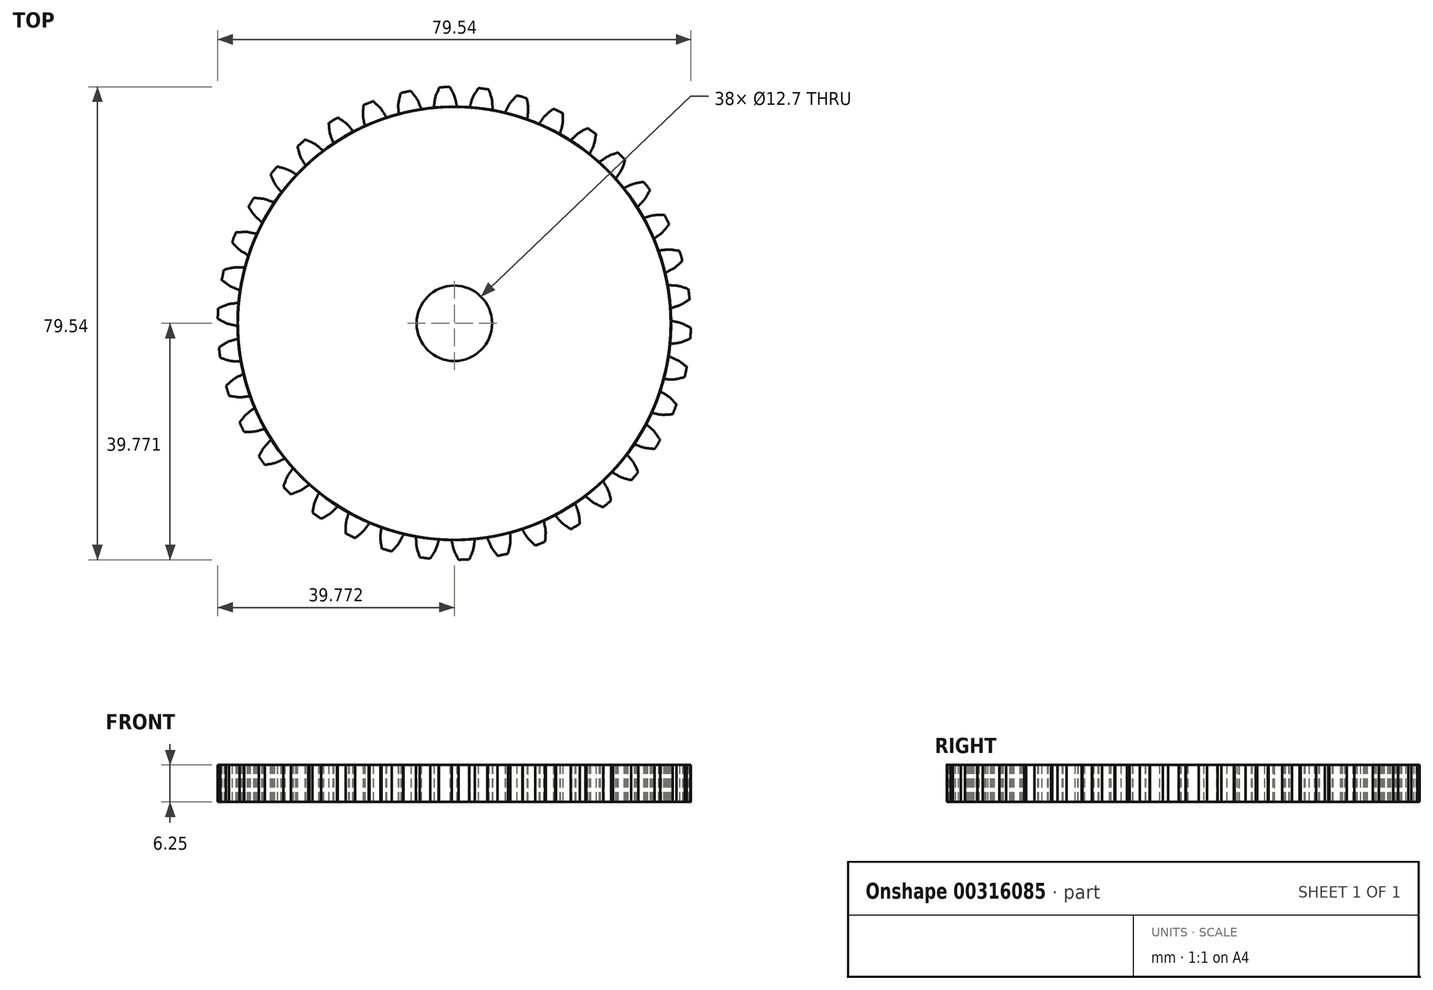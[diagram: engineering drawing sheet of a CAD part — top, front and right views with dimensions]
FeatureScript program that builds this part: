
annotation { "Feature Type Name" : "Feature", "Feature Type Description" : "" }
export const myFeature = defineFeature(function(context is Context, id is Id, definition is map)
    precondition{}
    {
        {
            var Q0;
            Q0=qCreatedBy(makeId("Top.planeOp"),FACE);
            var sketch = newSketch(context, id + "F0", { "sketchPlane" : qUnion([Q0])});
            skCircle(sketch, "E0", {"center": v(0, 0) * mm, "radius": 38.1 * mm, "construction": true});
            skLineSegment(sketch, "E1", {"start": v(0, 0) * mm, "end": v(0, 54.47) * mm, "construction": true});
            skLineSegment(sketch, "E2", {"start": v(-40.8, 38.1) * mm, "end": v(45.04, 38.1) * mm, "construction": true});
            skLineSegment(sketch, "E3", {"start": v(-12.24, 33.64) * mm, "end": v(18.8, 44.94) * mm, "construction": true});
            skLineSegment(sketch, "E4", {"start": v(0, 0) * mm, "end": v(-12.24, 33.64) * mm, "construction": true});
            skCircle(sketch, "E5", {"center": v(0, 0) * mm, "radius": 35.8 * mm, "construction": true});
            skPoint(sketch, "E6", {"position": v(-12.24, 33.64) * mm});
            skPoint(sketch, "E7", {"position": v(0, 38.1) * mm});
            skPoint(sketch, "E8", {"position": v(-16.8, 31.61) * mm});
            skLineSegment(sketch, "E9", {"start": v(-16.8, 31.61) * mm, "end": v(-0.9, 40.1) * mm, "construction": true});
            skArc(sketch, "E10", {"start": v(-7.44, 35.02) * mm, "mid": v(-9.87, 34.42) * mm, "end": v(-12.24, 33.64) * mm});
            skArc(sketch, "E11", {"start": v(-12.24, 33.64) * mm, "mid": v(-14.56, 32.7) * mm, "end": v(-16.8, 31.61) * mm});
            skLineSegment(sketch, "E12", {"start": v(-7.44, 35.02) * mm, "end": v(0.41, 36.69) * mm, "construction": true});
            skLineSegment(sketch, "E13", {"start": v(0, 38.1) * mm, "end": v(0, 0) * mm, "construction": true});
            skLineSegment(sketch, "E14", {"start": v(0.41, 36.69) * mm, "end": v(0.43, 36.44) * mm});
            skLineSegment(sketch, "E15.trimOffspring", {"start": v(0, 36.44) * mm, "end": v(0, 36.44) * mm});
            skLineSegment(sketch, "E16", {"start": v(0, 0) * mm, "end": v(-1.9, 46.38) * mm, "construction": true});
            skLineSegment(sketch, "E17.0.MirrorCS", {"start": v(5.36, 0.33) * mm, "end": v(1.52, 46.59) * mm, "construction": true});
            skLineSegment(sketch, "E18.0.MirrorCS", {"start": v(-3.43, 36.53) * mm, "end": v(-3.42, 36.28) * mm});
            skArc(sketch, "E19.converted", {"start": v(-3.42, 36.28) * mm, "mid": v(1.5, -36.41) * mm, "end": v(0.43, 36.44) * mm});
            skLineSegment(sketch, "E20", {"start": v(-3.42, 36.28) * mm, "end": v(-3.42, 36.28) * mm});
            skLineSegment(sketch, "E21", {"start": v(0.43, 36.44) * mm, "end": v(0.43, 36.44) * mm});
            skArc(sketch, "E22.trimOffspring", {"start": v(0.43, 36.44) * mm, "mid": v(-1.5, 36.41) * mm, "end": v(-3.42, 36.28) * mm});
            skArc(sketch, "E23.0", {"start": v(-0.74, 39.77) * mm, "mid": v(-1.64, 39.74) * mm, "end": v(-2.53, 39.7) * mm});
            skFitSpline(sketch, "E24.trimOffspring", {"points": [v(-2.4, 40.03) * mm, v(-3.13, 37.97) * mm, v(-3.43, 36.53) * mm], "startDerivative": vector(-1.5, -3.87) * mm, "endDerivative": vector(-0.5, -3.06) * mm});
            skFitSpline(sketch, "E25.trimOffspring", {"points": [v(-0.9, 40.1) * mm, v(0, 38.1) * mm, v(0.41, 36.69) * mm], "startDerivative": vector(1.82, -3.74) * mm, "endDerivative": vector(0.75, -3.01) * mm});
            skPoint(sketch, "E26.start.orphan", {"position": v(-0.86, 40.02) * mm});
            skPoint(sketch, "E27.trimOffspring.end.orphan", {"position": v(-2.43, 39.95) * mm});
            skCircle(sketch, "E28", {"center": v(0, 0) * mm, "radius": 6.35 * mm});
            skSolve(sketch);
        }
        {
            var Q0;
            Q0=qCreatedBy(makeId("Top.planeOp"),FACE);
            var sketch = newSketch(context, id + "F1", { "sketchPlane" : qUnion([Q0])});
            skFitSpline(sketch, "E29.0", {"points": [v(-2.4, 40.03) * mm, v(-2.68, 39.32) * mm, v(-3.18, 38.02) * mm, v(-3.35, 37) * mm, v(-3.43, 36.53) * mm]});
            skFitSpline(sketch, "E30.0", {"points": [v(-0.9, 40.1) * mm, v(-0.56, 39.4) * mm, v(0.05, 38.15) * mm, v(0.3, 37.14) * mm, v(0.41, 36.69) * mm]});
            skLineSegment(sketch, "E30.1", {"start": v(0.41, 36.69) * mm, "end": v(0.43, 36.44) * mm});
            skLineSegment(sketch, "E30.2", {"start": v(-3.43, 36.53) * mm, "end": v(-3.42, 36.28) * mm});
            skArc(sketch, "E30.3", {"start": v(-0.74, 39.77) * mm, "mid": v(-1.64, 39.74) * mm, "end": v(-2.53, 39.7) * mm});
            skArc(sketch, "E31.0", {"start": v(-3.42, 36.28) * mm, "mid": v(1.5, -36.41) * mm, "end": v(0.43, 36.44) * mm});
            skSolve(sketch);
        }
        {
            var Q0;
            Q0=makeQuery(id+"F1.imprint","IMPRINT",FACE,{"disambiguationData":[TD([[makeQuery(id+"F1.imprint","IMPRINT",EDGE,{"derivedFrom":sQuery(id+"F1.wireOp",EDGE,"E29.0")}),1.0]])]});
            extrude(context, id + "F2", {"entities" : qUnion([Q0]), "depth" : 25 / 4 * mm});
        }
        {
            var Q0;
            Q0=makeQuery(id+"F2.opExtrude","CAP_FACE",FACE,{"disambiguationData":[OSD([sQuery(id+"F1.wireOp",EDGE,"E29.0"),sQuery(id+"F1.wireOp",EDGE,"E30.0"),sQuery(id+"F1.wireOp",EDGE,"E30.1"),sQuery(id+"F1.wireOp",EDGE,"E30.2"),sQuery(id+"F1.wireOp",EDGE,"E30.3"),sQuery(id+"F1.wireOp",EDGE,"E31.0")])],"isStart":false});
            var Q1;
            Q1=makeQuery(id+"F2.opExtrude","SWEPT_BODY",BODY,{"disambiguationData":[OSD([sQuery(id+"F1.wireOp",EDGE,"E29.0"),sQuery(id+"F1.wireOp",EDGE,"E30.0"),sQuery(id+"F1.wireOp",EDGE,"E30.1"),sQuery(id+"F1.wireOp",EDGE,"E30.2"),sQuery(id+"F1.wireOp",EDGE,"E30.3"),sQuery(id+"F1.wireOp",EDGE,"E31.0")])]});
            var Q2;
            Q2=sQuery(id+"F1.wireOp",EDGE,"E31.0");
            circularPattern(context, id + "F3", {"entities" : qUnion([Q1]), "axis" : qUnion([Q2]), "angle" : 360 * degree, "instanceCount" : 38, "equalSpace" : true});
        }
        {
            var Q0;
            Q0=makeQuery(id+"F0.imprint","IMPRINT",FACE,{"disambiguationData":[TD([[makeQuery(id+"F0.imprint","IMPRINT",EDGE,{"derivedFrom":sQuery(id+"F0.wireOp",EDGE,"E28")}),1.0]])]});
            extrude(context, id + "F4", {"entities" : qUnion([Q0]), "operationType" : NewBodyOperationType.REMOVE, "depth" : 25 * mm});
        }
    });
